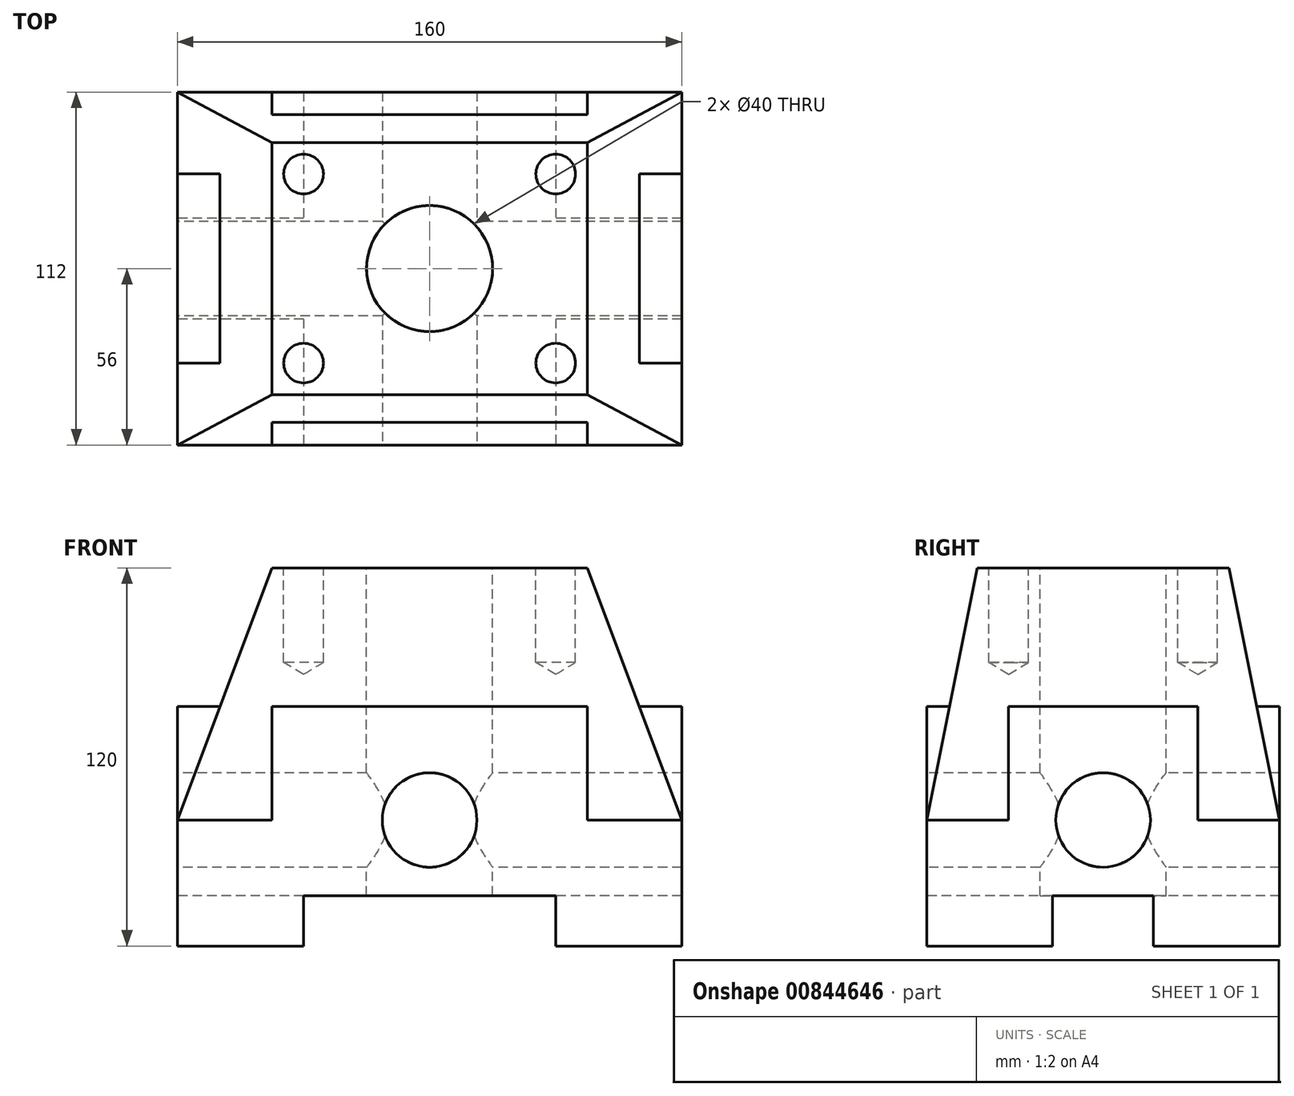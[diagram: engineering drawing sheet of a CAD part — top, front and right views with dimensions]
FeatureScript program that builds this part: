
annotation { "Feature Type Name" : "Feature", "Feature Type Description" : "" }
export const myFeature = defineFeature(function(context is Context, id is Id, definition is map)
    precondition{}
    {
        {
            var Q0;
            Q0=qCreatedBy(makeId("Top.planeOp"),FACE);
            var sketch = newSketch(context, id + "F0", { "sketchPlane" : qUnion([Q0])});
            skLineSegment(sketch, "E0.bottom", {"start": v(80, 56) * mm, "end": v(-80, 56) * mm});
            skLineSegment(sketch, "E0.top", {"start": v(80, -56) * mm, "end": v(-80, -56) * mm});
            skLineSegment(sketch, "E0.left", {"start": v(80, 56) * mm, "end": v(80, -56) * mm});
            skLineSegment(sketch, "E0.right", {"start": v(-80, 56) * mm, "end": v(-80, -56) * mm});
            skPoint(sketch, "E0.middle", {"position": v(0, 0) * mm});
            skSolve(sketch);
        }
        {
            var Q0;
            Q0=qSketchRegion(id+"F0",true);
            extrude(context, id + "F1", {"entities" : qUnion([Q0]), "oppositeDirection" : true, "depth" : 40 * mm, "offsetDistance" : 25 * mm});
        }
        {
            var Q0;
            Q0=makeQuery(id+"F1.opExtrude","SWEPT_FACE",FACE,{"disambiguationData":[OSD([sQuery(id+"F0.wireOp",EDGE,"E0.top")])]});
            var sketch = newSketch(context, id + "F2", { "sketchPlane" : qUnion([Q0])});
            skLineSegment(sketch, "E1.bottom", {"start": v(-40, -40) * mm, "end": v(40, -40) * mm});
            skLineSegment(sketch, "E1.top", {"start": v(-40, -24) * mm, "end": v(40, -24) * mm});
            skLineSegment(sketch, "E1.left", {"start": v(-40, -40) * mm, "end": v(-40, -24) * mm});
            skLineSegment(sketch, "E1.right", {"start": v(40, -40) * mm, "end": v(40, -24) * mm});
            skSolve(sketch);
        }
        {
            var Q0;
            Q0=qSketchRegion(id+"F2",true);
            extrude(context, id + "F3", {"entities" : qUnion([Q0]), "operationType" : NewBodyOperationType.REMOVE, "oppositeDirection" : true, "depth" : 115 * mm, "offsetDistance" : 25 * mm});
        }
        {
            var Q0;
            Q0=makeQuery(id+"F1.opExtrude","SWEPT_FACE",FACE,{"disambiguationData":[OSD([sQuery(id+"F0.wireOp",EDGE,"E0.right")])]});
            var sketch = newSketch(context, id + "F4", { "sketchPlane" : qUnion([Q0])});
            skLineSegment(sketch, "E2.bottom", {"start": v(-16, -40) * mm, "end": v(16, -40) * mm});
            skLineSegment(sketch, "E2.top", {"start": v(-16, -24) * mm, "end": v(16, -24) * mm});
            skLineSegment(sketch, "E2.left", {"start": v(-16, -40) * mm, "end": v(-16, -24) * mm});
            skLineSegment(sketch, "E2.right", {"start": v(16, -40) * mm, "end": v(16, -24) * mm});
            skSolve(sketch);
        }
        {
            var Q0;
            Q0=qSketchRegion(id+"F4",true);
            extrude(context, id + "F5", {"entities" : qUnion([Q0]), "operationType" : NewBodyOperationType.REMOVE, "oppositeDirection" : true, "depth" : 165 * mm, "offsetDistance" : 25 * mm});
        }
        {
            var Q0;
            Q0=makeQuery(id+"F1.opExtrude","CAP_FACE",FACE,{"disambiguationData":[OSD([sQuery(id+"F0.wireOp",EDGE,"E0.bottom"),sQuery(id+"F0.wireOp",EDGE,"E0.top"),sQuery(id+"F0.wireOp",EDGE,"E0.left"),sQuery(id+"F0.wireOp",EDGE,"E0.right")])],"isStart":true});
            var sketch = newSketch(context, id + "F6", { "sketchPlane" : qUnion([Q0])});
            skLineSegment(sketch, "E3.bottom", {"start": v(-50, 56) * mm, "end": v(50, 56) * mm});
            skLineSegment(sketch, "E3.top", {"start": v(-50, -56) * mm, "end": v(50, -56) * mm});
            skLineSegment(sketch, "E3.left", {"start": v(-50, 56) * mm, "end": v(-50, -56) * mm});
            skLineSegment(sketch, "E3.right", {"start": v(50, 56) * mm, "end": v(50, -56) * mm});
            skSolve(sketch);
        }
        {
            var Q0;
            Q0=qSketchRegion(id+"F6",true);
            extrude(context, id + "F7", {"entities" : qUnion([Q0]), "operationType" : NewBodyOperationType.ADD, "depth" : 36 * mm, "offsetDistance" : 25 * mm});
        }
        {
            var Q0;
            {var subQ0=sQuery(id+"F0.wireOp",EDGE,"E0.bottom");var subQ1=sQuery(id+"F0.wireOp",EDGE,"E0.left");var subQ2=sQuery(id+"F0.wireOp",EDGE,"E0.top");Q0=makeQuery(id+"F7.boolean.opBoolean","SPLIT",FACE,{"disambiguationData":[TD([makeQuery(id+"F1.opExtrude","SWEPT_FACE",FACE,{"disambiguationData":[OSD([subQ1])]})])],"derivedFrom":makeQuery(id+"F1.opExtrude","CAP_FACE",FACE,{"disambiguationData":[OSD([subQ0,subQ2,subQ1,sQuery(id+"F0.wireOp",EDGE,"E0.right")])],"isStart":true})});}
            var sketch = newSketch(context, id + "F8", { "sketchPlane" : qUnion([Q0])});
            skLineSegment(sketch, "E4.bottom", {"start": v(50, 30) * mm, "end": v(80, 30) * mm});
            skLineSegment(sketch, "E4.top", {"start": v(50, -30) * mm, "end": v(80, -30) * mm});
            skLineSegment(sketch, "E4.left", {"start": v(50, 30) * mm, "end": v(50, -30) * mm});
            skLineSegment(sketch, "E4.right", {"start": v(80, 30) * mm, "end": v(80, -30) * mm});
            skSolve(sketch);
        }
        {
            var Q0;
            Q0=qSketchRegion(id+"F8",true);
            extrude(context, id + "F9", {"entities" : qUnion([Q0]), "operationType" : NewBodyOperationType.ADD, "depth" : 36 * mm, "offsetDistance" : 25 * mm});
        }
        {
            var Q0;
            {var subQ0=sQuery(id+"F0.wireOp",EDGE,"E0.bottom");var subQ1=sQuery(id+"F0.wireOp",EDGE,"E0.top");var subQ2=sQuery(id+"F0.wireOp",EDGE,"E0.right");Q0=makeQuery(id+"F7.boolean.opBoolean","SPLIT",FACE,{"disambiguationData":[TD([makeQuery(id+"F1.opExtrude","SWEPT_FACE",FACE,{"disambiguationData":[OSD([subQ2])]})])],"derivedFrom":makeQuery(id+"F1.opExtrude","CAP_FACE",FACE,{"disambiguationData":[OSD([subQ0,subQ1,sQuery(id+"F0.wireOp",EDGE,"E0.left"),subQ2])],"isStart":true})});}
            var sketch = newSketch(context, id + "F10", { "sketchPlane" : qUnion([Q0])});
            skLineSegment(sketch, "E5.bottom", {"start": v(-80, 30) * mm, "end": v(-50, 30) * mm});
            skLineSegment(sketch, "E5.top", {"start": v(-80, -30) * mm, "end": v(-50, -30) * mm});
            skLineSegment(sketch, "E5.left", {"start": v(-80, 30) * mm, "end": v(-80, -30) * mm});
            skLineSegment(sketch, "E5.right", {"start": v(-50, 30) * mm, "end": v(-50, -30) * mm});
            skSolve(sketch);
        }
        {
            var Q0;
            Q0=qSketchRegion(id+"F10",true);
            extrude(context, id + "F11", {"entities" : qUnion([Q0]), "operationType" : NewBodyOperationType.ADD, "depth" : 36 * mm, "offsetDistance" : 25 * mm});
        }
        {
            var Q0;
            Q0=qCreatedBy(makeId("Top.planeOp"),FACE);
            var sketch = newSketch(context, id + "F12", { "sketchPlane" : qUnion([Q0])});
            skLineSegment(sketch, "E6.bottom", {"start": v(80, 56) * mm, "end": v(-80, 56) * mm});
            skLineSegment(sketch, "E6.top", {"start": v(80, -56) * mm, "end": v(-80, -56) * mm});
            skLineSegment(sketch, "E6.left", {"start": v(80, 56) * mm, "end": v(80, -56) * mm});
            skLineSegment(sketch, "E6.right", {"start": v(-80, 56) * mm, "end": v(-80, -56) * mm});
            skPoint(sketch, "E6.middle", {"position": v(0, 0) * mm});
            skSolve(sketch);
        }
        {
            var Q0;
            Q0=qCreatedBy(makeId("Top.planeOp"),FACE);
            cPlane(context, id + "F13", {"entities" : qUnion([Q0]), "cplaneType" : CPlaneType.OFFSET, "offset" : 80 * mm, "width" : 150 * mm, "height" : 150 * mm});
        }
        {
            var Q0;
            Q0=qCreatedBy(id+"F13.planeOp",FACE);
            var sketch = newSketch(context, id + "F14", { "sketchPlane" : qUnion([Q0])});
            skLineSegment(sketch, "E7.bottom", {"start": v(50, 40) * mm, "end": v(-50, 40) * mm});
            skLineSegment(sketch, "E7.top", {"start": v(50, -40) * mm, "end": v(-50, -40) * mm});
            skLineSegment(sketch, "E7.left", {"start": v(50, 40) * mm, "end": v(50, -40) * mm});
            skLineSegment(sketch, "E7.right", {"start": v(-50, 40) * mm, "end": v(-50, -40) * mm});
            skPoint(sketch, "E7.middle", {"position": v(0, 0) * mm});
            skSolve(sketch);
        }
        {
            var Q1;
            Q1=makeQuery(id+"F14.imprint","IMPRINT",FACE,{"disambiguationData":[TD([[makeQuery(id+"F14.imprint","IMPRINT",EDGE,{"derivedFrom":sQuery(id+"F14.wireOp",EDGE,"E7.bottom")}),1.0]])]});
            var Q2;
            Q2=makeQuery(id+"F12.imprint","IMPRINT",FACE,{"disambiguationData":[TD([[makeQuery(id+"F12.imprint","IMPRINT",EDGE,{"derivedFrom":sQuery(id+"F12.wireOp",EDGE,"E6.bottom")}),1.0]])]});
            loft(context, id + "F15", {"operationType" : NewBodyOperationType.ADD, "sheetProfilesArray" : [{ "sheetProfileEntities" : qUnion([Q1]) }, { "sheetProfileEntities" : qUnion([Q2]) }]});
        }
        {
            var Q0;
            Q0=makeQuery(id+"F15.opLoft","CAP_FACE",FACE,{"disambiguationData":[OSD([makeQuery(id+"F14.imprint","IMPRINT",FACE,{"disambiguationData":[TD([[makeQuery(id+"F14.imprint","IMPRINT",EDGE,{"derivedFrom":sQuery(id+"F14.wireOp",EDGE,"E7.bottom")}),1.0]])]})])],"isStart":true});
            var sketch = newSketch(context, id + "F16", { "sketchPlane" : qUnion([Q0])});
            skCircle(sketch, "E8", {"center": v(0, 0) * mm, "radius": 20 * mm});
            skSolve(sketch);
        }
        {
            var Q0;
            Q0=qSketchRegion(id+"F16",true);
            extrude(context, id + "F17", {"entities" : qUnion([Q0]), "operationType" : NewBodyOperationType.REMOVE, "oppositeDirection" : true, "depth" : 120 * mm, "offsetDistance" : 25 * mm});
        }
        {
            var Q0;
            Q0=makeQuery(id+"F7.boolean.opBoolean","MERGE",FACE,{"derivedFrom":[makeQuery(id+"F1.opExtrude","SWEPT_FACE",FACE,{"disambiguationData":[OSD([sQuery(id+"F0.wireOp",EDGE,"E0.top")])]}),makeQuery(id+"F7.opExtrude","SWEPT_FACE",FACE,{"disambiguationData":[OSD([sQuery(id+"F6.wireOp",EDGE,"E3.top")])]})]});
            var sketch = newSketch(context, id + "F18", { "sketchPlane" : qUnion([Q0])});
            skCircle(sketch, "E9", {"center": v(0, 0) * mm, "radius": 15 * mm});
            skSolve(sketch);
        }
        {
            var Q0;
            Q0=qSketchRegion(id+"F18",true);
            extrude(context, id + "F19", {"entities" : qUnion([Q0]), "operationType" : NewBodyOperationType.REMOVE, "oppositeDirection" : true, "depth" : 112 * mm, "offsetDistance" : 25 * mm});
        }
        {
            var Q0;
            Q0=makeQuery(id+"F11.boolean.opBoolean","MERGE",FACE,{"derivedFrom":[makeQuery(id+"F1.opExtrude","SWEPT_FACE",FACE,{"disambiguationData":[OSD([sQuery(id+"F0.wireOp",EDGE,"E0.right")])]}),makeQuery(id+"F11.opExtrude","SWEPT_FACE",FACE,{"disambiguationData":[OSD([sQuery(id+"F10.wireOp",EDGE,"E5.left")])]})]});
            var sketch = newSketch(context, id + "F20", { "sketchPlane" : qUnion([Q0])});
            skCircle(sketch, "E10", {"center": v(0, 0) * mm, "radius": 15 * mm});
            skSolve(sketch);
        }
        {
            var Q0;
            Q0=qSketchRegion(id+"F20",true);
            extrude(context, id + "F21", {"entities" : qUnion([Q0]), "operationType" : NewBodyOperationType.REMOVE, "oppositeDirection" : true, "depth" : 160 * mm, "offsetDistance" : 25 * mm});
        }
        {
            var Q0;
            Q0=makeQuery(id+"F15.opLoft","CAP_FACE",FACE,{"disambiguationData":[OSD([makeQuery(id+"F14.imprint","IMPRINT",FACE,{"disambiguationData":[TD([[makeQuery(id+"F14.imprint","IMPRINT",EDGE,{"derivedFrom":sQuery(id+"F14.wireOp",EDGE,"E7.bottom")}),1.0]])]})])],"isStart":true});
            var sketch = newSketch(context, id + "F22", { "sketchPlane" : qUnion([Q0])});
            skPoint(sketch, "E11", {"position": v(-40, 30) * mm});
            skPoint(sketch, "E12", {"position": v(40, 30) * mm});
            skPoint(sketch, "E13", {"position": v(40, -30) * mm});
            skPoint(sketch, "E14", {"position": v(-40, -30) * mm});
            skSolve(sketch);
        }
        {
            var Q0;
            Q0=sQuery(id+"F22.wireOp",VERTEX,"E11");
            var Q1;
            Q1=sQuery(id+"F22.wireOp",VERTEX,"E12");
            var Q2;
            Q2=sQuery(id+"F22.wireOp",VERTEX,"E13");
            var Q3;
            Q3=sQuery(id+"F22.wireOp",VERTEX,"E14");
            var Q4;
            Q4=makeQuery(id+"F1.opExtrude","SWEPT_BODY",BODY,{"disambiguationData":[OSD([sQuery(id+"F0.wireOp",EDGE,"E0.bottom"),sQuery(id+"F0.wireOp",EDGE,"E0.top"),sQuery(id+"F0.wireOp",EDGE,"E0.left"),sQuery(id+"F0.wireOp",EDGE,"E0.right")])]});
            hole(context, id + "F23", {"style" : HoleStyle.SIMPLE, "endStyle" : HoleEndStyle.BLIND, "standardTappedOrClearance" : lookupTablePath({ "fit" : "Close", "standard" : "ISO", "size" : "M12", "type" : "Clearance" }), "standardBlindInLast" : lookupTablePath({ "fit" : "Close", "standard" : "ISO", "size" : "M12", "type" : "Clearance" }), "holeDiameter" : 12.6 * mm, "majorDiameter" : 5 * mm, "holeDepth" : 30 * mm, "isTappedThrough" : true, "tappedDepth" : 12 * mm, "tapClearance" : 3, "startFromSketch" : true, "locations" : qUnion([Q0, Q1, Q2, Q3]), "scope" : qUnion([Q4])});
        }
    });
